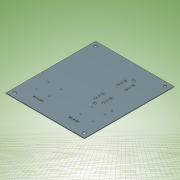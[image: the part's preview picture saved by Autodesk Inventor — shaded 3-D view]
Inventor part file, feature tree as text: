
AUTODESK INVENTOR PART (.ipt)
format: ipt  version: 2022 (Build 260153000, 153)  size: 288,256 bytes
history: native  units: mm
features: other x1, extrude x1, sketch x1
ambient origin geometry x8: Origin, YZ Plane, XZ Plane, XY Plane, X Axis, Y Axis, Z Axis, Center Point
bodies: Body1 (feature_tree)
feature tree (3):
  other  "Sólido1"
  extrude  "Extrusión1"  Depth=400.0mm
  sketch  "Boceto1"  dims[d0=350.0mm d1=400.0mm d2=3.0mm d3=0.0mm d4=12.0mm d5=20.0mm d6=20.0mm d7=5.0mm d8=5.0mm d11=10.0mm d12=6.0mm d13=10.0mm d15=18.0mm d16=6.0mm d17=9.011mm d18=10.0mm d19=6.0mm d20=10.0mm d21=6.0mm d22=18.0mm d23=9.011mm d26=121.023mm d27=45.0mm d29=15.0mm d30=250.0mm d31=5.0mm d33=10.0mm d34=6.0mm d35=10.0mm d36=20.0mm d37=10.0mm d39=10.0mm d40=60.0mm d41=6.0mm d42=5.0mm d43=10.0mm d44=6.0mm d45=10.0mm d46=20.0mm d48=10.0mm d50=42.0mm d51=6.0mm d52=6.0mm d53=5.0mm d54=6.0mm d55=10.0mm d56=5.0mm d57=20.0mm d58=10.0mm d59=6.0mm d60=10.0mm d61=10.0mm d62=6.0mm d64=16.0mm d66=10.0mm d67=6.0mm d68=16.0mm d70=20.0mm d71=20.0mm d73=20.0mm d77=20.0mm d81=65.0mm d82=60.0mm d83=5.0mm d84=11.34178mm d85=48.0mm d86=4.0mm d87=3.683mm d88=2.921mm d89=4.0mm d90=3.556mm d91=2.921mm d92=4.0mm d93=3.556mm d94=3.683mm d95=4.0mm d96=3.683mm d97=3.683mm d98=80.0mm d99=65.0mm d100=60.0mm d101=4.0mm d102=3.683mm d103=2.921mm d104=4.0mm d105=3.556mm d106=2.921mm d107=4.0mm d108=3.556mm d109=3.683mm d110=4.0mm d111=3.683mm d112=3.683mm d113=130.0mm]
